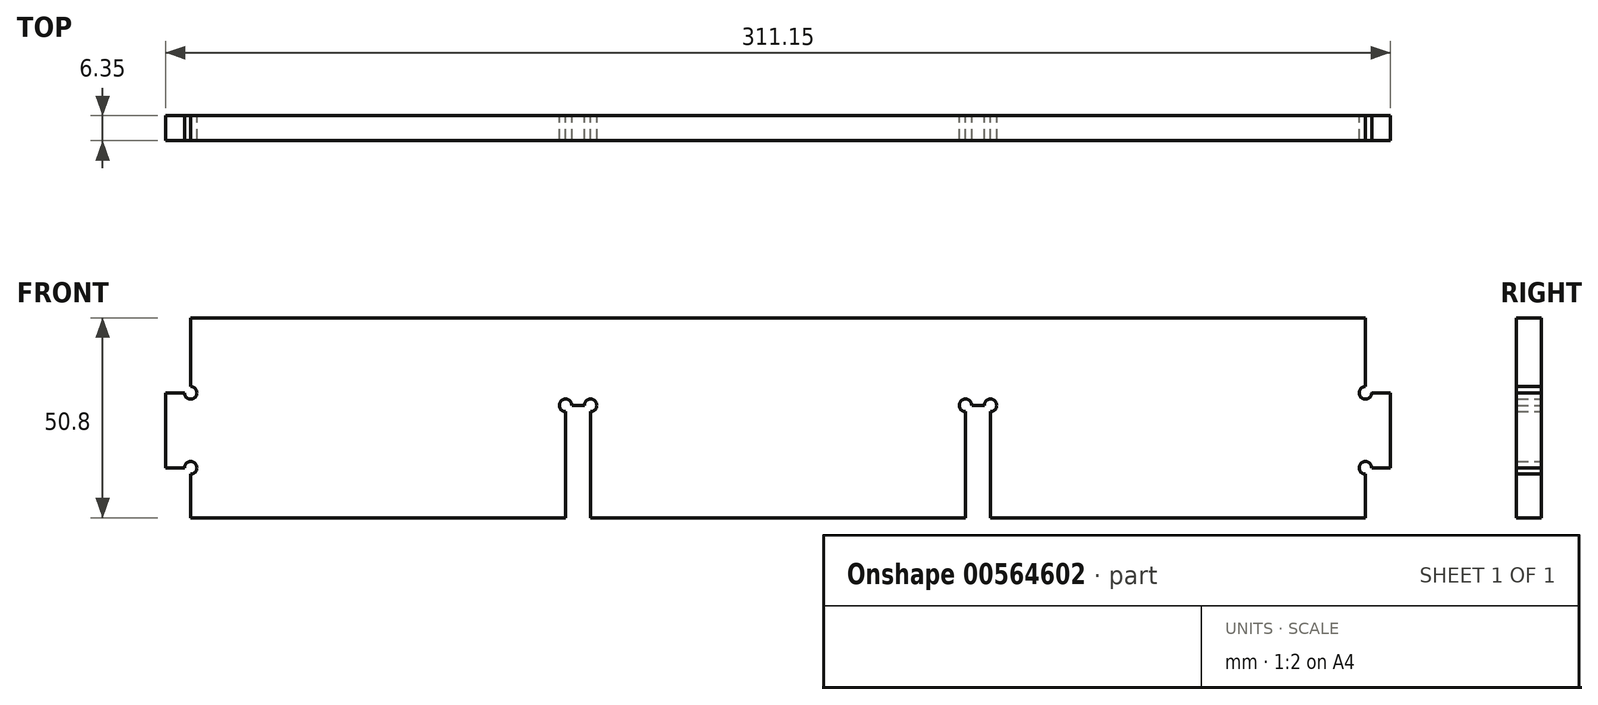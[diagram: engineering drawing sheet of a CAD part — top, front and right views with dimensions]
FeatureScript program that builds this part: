
annotation { "Feature Type Name" : "Feature", "Feature Type Description" : "" }
export const myFeature = defineFeature(function(context is Context, id is Id, definition is map)
    precondition{}
    {
        {
            var Q0;
            Q0=qCreatedBy(makeId("Front.planeOp"),FACE);
            var sketch = newSketch(context, id + "F0", { "sketchPlane" : qUnion([Q0])});
            skLineSegment(sketch, "E0.bottom", {"start": v(-151.54, 21.9) * mm, "end": v(146.91, 21.9) * mm});
            skLineSegment(sketch, "E0.top", {"start": v(-151.54, -28.9) * mm, "end": v(146.91, -28.9) * mm});
            skLineSegment(sketch, "E0.left", {"start": v(-151.54, 21.9) * mm, "end": v(-151.54, -28.9) * mm});
            skLineSegment(sketch, "E0.right", {"start": v(146.91, 21.9) * mm, "end": v(146.91, -28.9) * mm});
            skLineSegment(sketch, "E1.bottom", {"start": v(-56.29, -28.9) * mm, "end": v(-49.94, -28.9) * mm});
            skLineSegment(sketch, "E1.top", {"start": v(-56.29, -0.32) * mm, "end": v(-49.94, -0.32) * mm});
            skLineSegment(sketch, "E1.left", {"start": v(-56.29, -28.9) * mm, "end": v(-56.29, -0.32) * mm});
            skLineSegment(sketch, "E1.right", {"start": v(-49.94, -28.9) * mm, "end": v(-49.94, -0.32) * mm});
            skLineSegment(sketch, "E2.bottom", {"start": v(51.66, -28.9) * mm, "end": v(45.31, -28.9) * mm});
            skLineSegment(sketch, "E2.top", {"start": v(51.66, -0.32) * mm, "end": v(45.31, -0.32) * mm});
            skLineSegment(sketch, "E2.left", {"start": v(51.66, -28.9) * mm, "end": v(51.66, -0.32) * mm});
            skLineSegment(sketch, "E2.right", {"start": v(45.31, -28.9) * mm, "end": v(45.31, -0.32) * mm});
            skLineSegment(sketch, "E3.left", {"start": v(-151.54, 21.9) * mm, "end": v(-151.54, 2.86) * mm});
            skLineSegment(sketch, "E4.left", {"start": v(-151.54, -16.2) * mm, "end": v(-151.54, -28.9) * mm});
            skLineSegment(sketch, "E5.left", {"start": v(146.91, 21.9) * mm, "end": v(146.91, 2.86) * mm});
            skLineSegment(sketch, "E6.left", {"start": v(146.91, -28.9) * mm, "end": v(146.91, -16.2) * mm});
            skLineSegment(sketch, "E7.bottom", {"start": v(146.91, 2.86) * mm, "end": v(153.26, 2.86) * mm});
            skLineSegment(sketch, "E7.top", {"start": v(146.91, -16.2) * mm, "end": v(153.26, -16.2) * mm});
            skLineSegment(sketch, "E7.left", {"start": v(146.91, 2.86) * mm, "end": v(146.91, -16.2) * mm});
            skLineSegment(sketch, "E7.right", {"start": v(153.26, 2.86) * mm, "end": v(153.26, -16.2) * mm});
            skLineSegment(sketch, "E8.bottom", {"start": v(-151.54, 2.86) * mm, "end": v(-157.89, 2.86) * mm});
            skLineSegment(sketch, "E8.top", {"start": v(-151.54, -16.2) * mm, "end": v(-157.89, -16.2) * mm});
            skLineSegment(sketch, "E8.left", {"start": v(-151.54, 2.86) * mm, "end": v(-151.54, -16.2) * mm});
            skLineSegment(sketch, "E8.right", {"start": v(-157.89, 2.86) * mm, "end": v(-157.89, -16.2) * mm});
            skPoint(sketch, "E9.visualSharp", {"position": v(-157.89, 2.86) * mm});
            skLineSegment(sketch, "E9.filletArc", {"start": v(-157.89, 2.86) * mm, "end": v(-157.89, 2.86) * mm});
            skPoint(sketch, "E10.visualSharp", {"position": v(-157.89, -16.2) * mm});
            skLineSegment(sketch, "E10.filletArc", {"start": v(-157.89, -16.2) * mm, "end": v(-157.89, -16.2) * mm});
            skPoint(sketch, "E11.visualSharp", {"position": v(-56.29, -0.32) * mm});
            skLineSegment(sketch, "E11.filletArc", {"start": v(-56.29, -0.32) * mm, "end": v(-56.29, -0.32) * mm});
            skPoint(sketch, "E12.visualSharp", {"position": v(-49.94, -0.32) * mm});
            skLineSegment(sketch, "E12.filletArc", {"start": v(-49.94, -0.32) * mm, "end": v(-49.94, -0.32) * mm});
            skPoint(sketch, "E13.visualSharp", {"position": v(45.31, -0.32) * mm});
            skLineSegment(sketch, "E13.filletArc", {"start": v(45.31, -0.32) * mm, "end": v(45.31, -0.32) * mm});
            skPoint(sketch, "E14.visualSharp", {"position": v(51.66, -0.32) * mm});
            skLineSegment(sketch, "E14.filletArc", {"start": v(51.66, -0.32) * mm, "end": v(51.66, -0.32) * mm});
            skPoint(sketch, "E15.visualSharp", {"position": v(153.26, 2.86) * mm});
            skLineSegment(sketch, "E15.filletArc", {"start": v(153.26, 2.86) * mm, "end": v(153.26, 2.86) * mm});
            skPoint(sketch, "E16.visualSharp", {"position": v(153.26, -16.2) * mm});
            skLineSegment(sketch, "E16.filletArc", {"start": v(153.26, -16.2) * mm, "end": v(153.26, -16.2) * mm});
            skCircle(sketch, "E17", {"center": v(-151.54, 2.86) * mm, "radius": 1.59 * mm});
            skCircle(sketch, "E18", {"center": v(-151.54, -16.2) * mm, "radius": 1.59 * mm});
            skCircle(sketch, "E19", {"center": v(-56.29, -0.32) * mm, "radius": 1.59 * mm});
            skCircle(sketch, "E20", {"center": v(-49.94, -0.32) * mm, "radius": 1.59 * mm});
            skCircle(sketch, "E21", {"center": v(45.31, -0.32) * mm, "radius": 1.59 * mm});
            skCircle(sketch, "E22", {"center": v(51.66, -0.32) * mm, "radius": 1.59 * mm});
            skCircle(sketch, "E23", {"center": v(146.91, 2.86) * mm, "radius": 1.59 * mm});
            skCircle(sketch, "E24", {"center": v(146.91, -16.2) * mm, "radius": 1.59 * mm});
            skSolve(sketch);
        }
        {
            var Q0;
            {var subQ22=sQuery(id+"F0.wireOp",EDGE,"E0.bottom");Q0=makeQuery(id+"F0.imprint","IMPRINT",FACE,{"disambiguationData":[TD([[makeQuery(id+"F0.imprint","IMPRINT",EDGE,{"derivedFrom":subQ22}),-1.0]])]});}
            var Q1;
            {var subQ0=sQuery(id+"F0.wireOp",EDGE,"E7.right");Q1=makeQuery(id+"F0.imprint","IMPRINT",FACE,{"disambiguationData":[TD([[makeQuery(id+"F0.imprint","IMPRINT",EDGE,{"derivedFrom":subQ0}),-1.0]])]});}
            var Q2;
            {var subQ0=sQuery(id+"F0.wireOp",EDGE,"E8.right");Q2=makeQuery(id+"F0.imprint","IMPRINT",FACE,{"disambiguationData":[TD([[makeQuery(id+"F0.imprint","IMPRINT",EDGE,{"derivedFrom":subQ0}),1.0]])]});}
            extrude(context, id + "F1", {"entities" : qUnion([Q0, Q1, Q2]), "depth" : 6.35 * mm, "offsetDistance" : 25.4 * mm});
        }
    });
